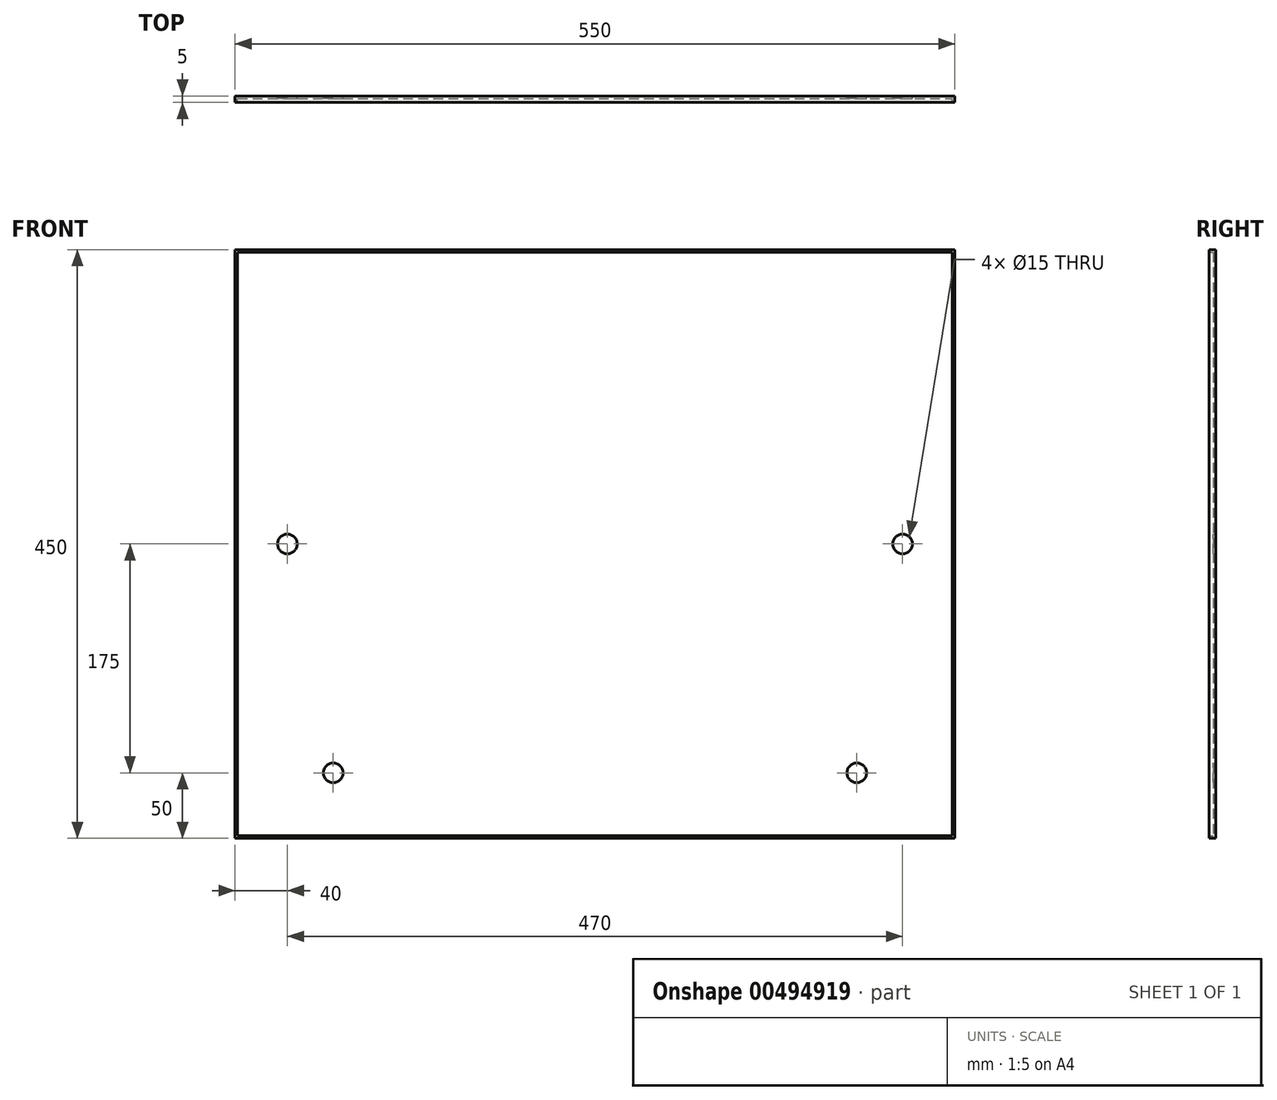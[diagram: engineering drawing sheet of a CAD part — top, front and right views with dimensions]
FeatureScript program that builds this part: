
annotation { "Feature Type Name" : "Feature", "Feature Type Description" : "" }
export const myFeature = defineFeature(function(context is Context, id is Id, definition is map)
    precondition{}
    {
        {
            var Q0;
            Q0=qCreatedBy(makeId("Front.planeOp"),FACE);
            var sketch = newSketch(context, id + "F0", { "sketchPlane" : qUnion([Q0])});
            skLineSegment(sketch, "E0.bottom", {"start": v(-275, 225) * mm, "end": v(275, 225) * mm});
            skLineSegment(sketch, "E0.top", {"start": v(-275, -225) * mm, "end": v(275, -225) * mm});
            skLineSegment(sketch, "E0.left", {"start": v(-275, 225) * mm, "end": v(-275, -225) * mm});
            skLineSegment(sketch, "E0.right", {"start": v(275, 225) * mm, "end": v(275, -225) * mm});
            skSolve(sketch);
        }
        {
            var Q0;
            Q0=qSketchRegion(id+"F0",true);
            extrude(context, id + "F1", {"entities" : qUnion([Q0]), "depth" : 5 * mm});
        }
        {
            var Q0;
            Q0=makeQuery(id+"F1.opExtrude","CAP_FACE",FACE,{"disambiguationData":[OSD([sQuery(id+"F0.wireOp",EDGE,"E0.bottom"),sQuery(id+"F0.wireOp",EDGE,"E0.top"),sQuery(id+"F0.wireOp",EDGE,"E0.left"),sQuery(id+"F0.wireOp",EDGE,"E0.right")])],"isStart":false});
            shell(context, id + "F2", {"entities" : qUnion([Q0]), "thickness" : 2 * mm});
        }
        {
            var Q0;
            Q0=makeQuery(id+"F1.opExtrude","CAP_FACE",FACE,{"disambiguationData":[OSD([sQuery(id+"F0.wireOp",EDGE,"E0.bottom"),sQuery(id+"F0.wireOp",EDGE,"E0.top"),sQuery(id+"F0.wireOp",EDGE,"E0.left"),sQuery(id+"F0.wireOp",EDGE,"E0.right")])],"isStart":true});
            var sketch = newSketch(context, id + "F3", { "sketchPlane" : qUnion([Q0])});
            skPoint(sketch, "E1", {"position": v(235, 0) * mm});
            skPoint(sketch, "E2", {"position": v(-235, 0) * mm});
            skPoint(sketch, "E3", {"position": v(-200, -175) * mm});
            skPoint(sketch, "E4", {"position": v(200, -175) * mm});
            skSolve(sketch);
        }
        {
            var Q0;
            Q0=sQuery(id+"F3.wireOp",VERTEX,"E1");
            var Q1;
            Q1=sQuery(id+"F3.wireOp",VERTEX,"E2");
            var Q2;
            Q2=sQuery(id+"F3.wireOp",VERTEX,"E3");
            var Q3;
            Q3=sQuery(id+"F3.wireOp",VERTEX,"E4");
            var Q4;
            Q4=makeQuery(id+"F1.opExtrude","SWEPT_BODY",BODY,{"disambiguationData":[OSD([sQuery(id+"F0.wireOp",EDGE,"E0.bottom"),sQuery(id+"F0.wireOp",EDGE,"E0.top"),sQuery(id+"F0.wireOp",EDGE,"E0.left"),sQuery(id+"F0.wireOp",EDGE,"E0.right")])]});
            hole(context, id + "F4", {"style" : HoleStyle.SIMPLE, "endStyle" : HoleEndStyle.THROUGH, "holeDiameter" : 15 * mm, "isTappedThrough" : true, "tappedDepth" : 15 * mm, "tapClearance" : 3, "locations" : qUnion([Q0, Q1, Q2, Q3]), "scope" : qUnion([Q4])});
        }
    });
